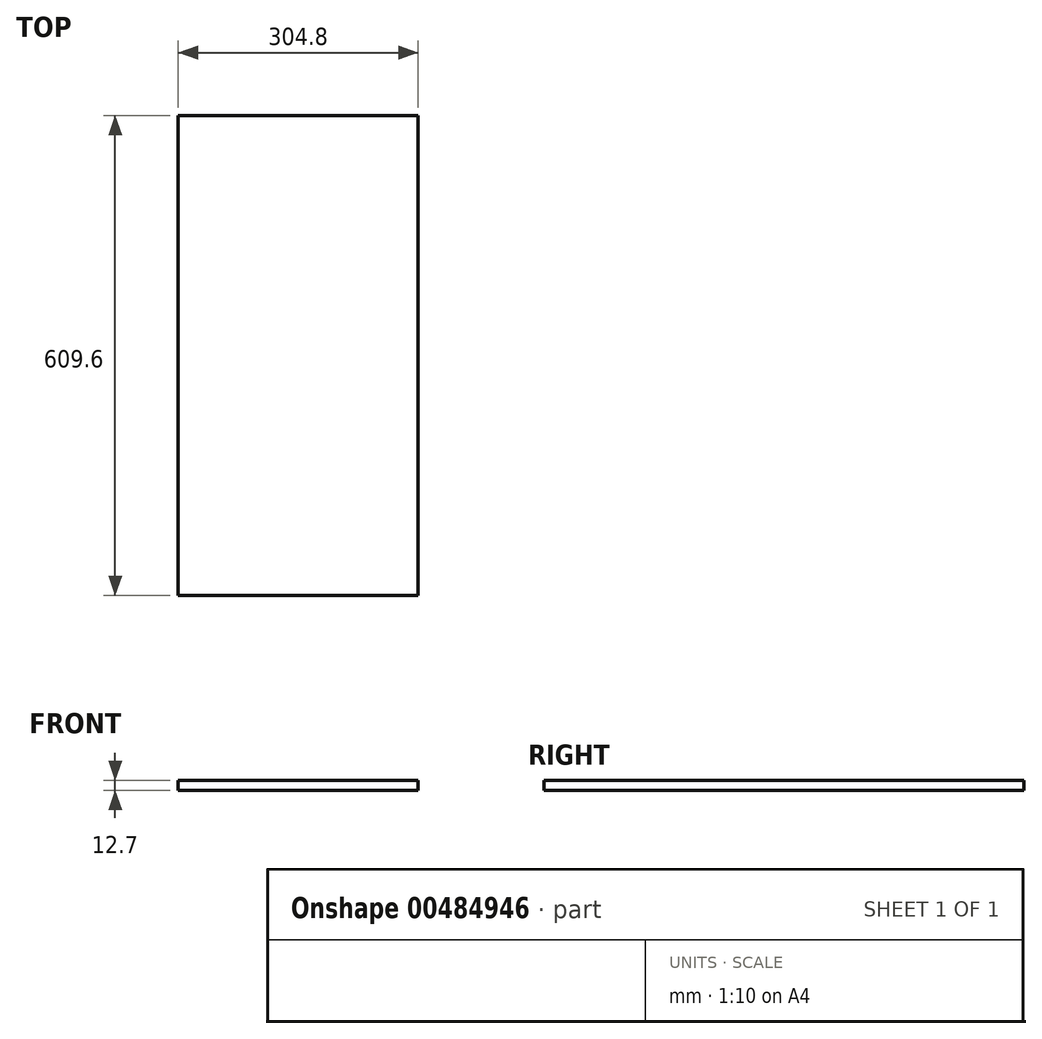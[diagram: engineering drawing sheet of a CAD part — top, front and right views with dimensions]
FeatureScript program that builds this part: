
annotation { "Feature Type Name" : "Feature", "Feature Type Description" : "" }
export const myFeature = defineFeature(function(context is Context, id is Id, definition is map)
    precondition{}
    {
        {
            var Q0;
            Q0=qCreatedBy(makeId("Top.planeOp"),FACE);
            var sketch = newSketch(context, id + "F0", { "sketchPlane" : qUnion([Q0])});
            skLineSegment(sketch, "E0.bottom", {"start": v(0, 0) * mm, "end": v(304.8, 0) * mm});
            skLineSegment(sketch, "E0.top", {"start": v(0, 609.6) * mm, "end": v(304.8, 609.6) * mm});
            skLineSegment(sketch, "E0.left", {"start": v(0, 0) * mm, "end": v(0, 609.6) * mm});
            skLineSegment(sketch, "E0.right", {"start": v(304.8, 0) * mm, "end": v(304.8, 609.6) * mm});
            skSolve(sketch);
        }
        {
            var Q0;
            Q0 = qSketchRegion(id + "F0", true);
            extrude(context, id + "F1", {"entities" : qUnion([Q0]), "depth" : 12.7 * mm});
        }
    });
